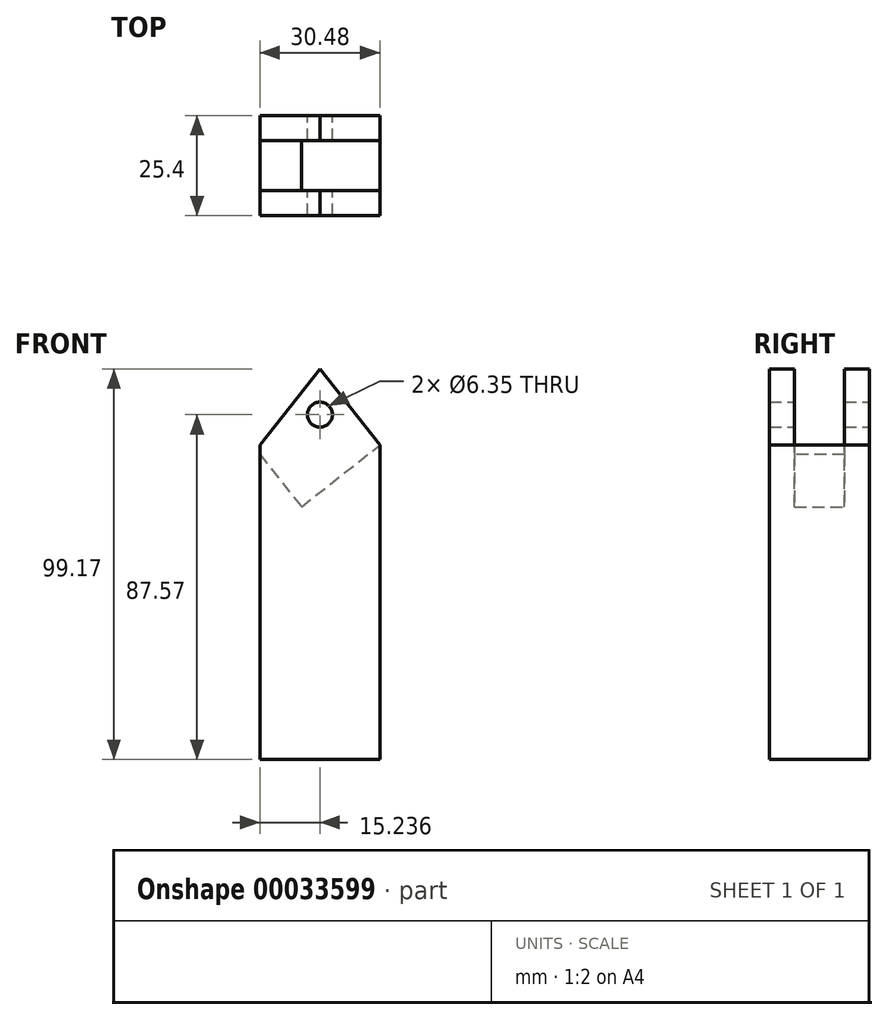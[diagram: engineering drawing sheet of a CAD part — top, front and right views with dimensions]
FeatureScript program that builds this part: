
annotation { "Feature Type Name" : "Feature", "Feature Type Description" : "" }
export const myFeature = defineFeature(function(context is Context, id is Id, definition is map)
    precondition{}
    {
        {
            var Q0;
            Q0=qCreatedBy(makeId("Front.planeOp"),FACE);
            var sketch = newSketch(context, id + "F0", { "sketchPlane" : qUnion([Q0])});
            skLineSegment(sketch, "E0.bottom", {"start": v(-50.65, 53.08) * mm, "end": v(-20.17, 53.08) * mm});
            skLineSegment(sketch, "E0.top", {"start": v(-50.65, -46.09) * mm, "end": v(-20.17, -46.09) * mm});
            skLineSegment(sketch, "E0.left", {"start": v(-50.65, 53.08) * mm, "end": v(-50.65, -46.09) * mm});
            skLineSegment(sketch, "E0.right", {"start": v(-20.17, 53.08) * mm, "end": v(-20.17, -46.09) * mm});
            skLineSegment(sketch, "E1", {"start": v(-35.41, 53.08) * mm, "end": v(-50.65, 33.8) * mm});
            skLineSegment(sketch, "E2", {"start": v(-35.41, 53.08) * mm, "end": v(-20.17, 33.8) * mm});
            skCircle(sketch, "E3", {"center": v(-35.41, 41.48) * mm, "radius": 3.18 * mm});
            skSolve(sketch);
        }
        {
            var Q0;
            {var subQ3=sQuery(id+"F0.wireOp",EDGE,"E0.top");Q0=makeQuery(id+"F0.imprint","IMPRINT",FACE,{"disambiguationData":[TD([[makeQuery(id+"F0.imprint","IMPRINT",EDGE,{"derivedFrom":subQ3}),1.0]])]});}
            extrude(context, id + "F1", {"entities" : qUnion([Q0]), "depth" : 25.4 * mm});
        }
        {
            var Q0;
            Q0=makeQuery(id+"F1.opExtrude","SWEPT_FACE",FACE,{"disambiguationData":[OSD([sQuery(id+"F0.wireOp",EDGE,"E2")])]});
            var sketch = newSketch(context, id + "F2", { "sketchPlane" : qUnion([Q0])});
            skLineSegment(sketch, "E4.bottom", {"start": v(-19.05, 63.6) * mm, "end": v(-6.35, 63.6) * mm});
            skLineSegment(sketch, "E4.top", {"start": v(-19.05, 39.03) * mm, "end": v(-6.35, 39.03) * mm});
            skLineSegment(sketch, "E4.left", {"start": v(-19.05, 63.6) * mm, "end": v(-19.05, 39.03) * mm});
            skLineSegment(sketch, "E4.right", {"start": v(-6.35, 63.6) * mm, "end": v(-6.35, 39.03) * mm});
            skPoint(sketch, "E5", {"position": v(-25.4, 63.6) * mm});
            skPoint(sketch, "E6", {"position": v(0, 63.6) * mm});
            skLineSegment(sketch, "E7", {"start": v(-19.05, 63.6) * mm, "end": v(-25.4, 63.6) * mm});
            skLineSegment(sketch, "E8", {"start": v(-6.35, 63.6) * mm, "end": v(0, 63.6) * mm});
            skSolve(sketch);
        }
        {
            var Q0;
            Q0=makeQuery(id+"F2.imprint","IMPRINT",FACE,{"disambiguationData":[TD([[makeQuery(id+"F2.imprint","IMPRINT",EDGE,{"derivedFrom":sQuery(id+"F2.wireOp",EDGE,"E4.bottom")}),-1.0]])]});
            extrude(context, id + "F3", {"entities" : qUnion([Q0]), "operationType" : NewBodyOperationType.REMOVE, "oppositeDirection" : true, "depth" : 25.4 * mm});
        }
    });
